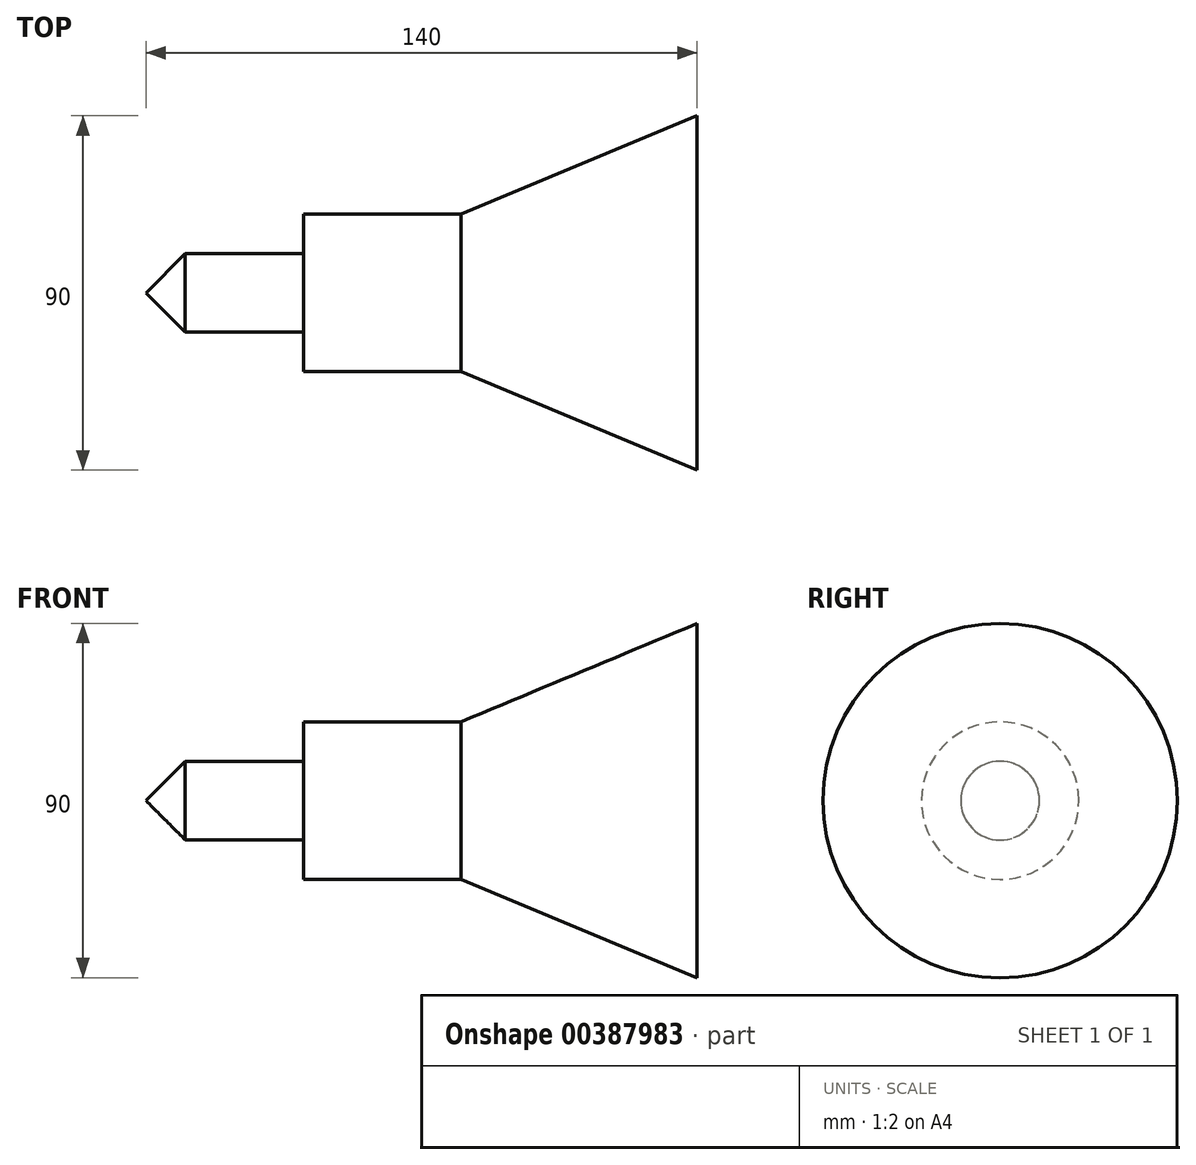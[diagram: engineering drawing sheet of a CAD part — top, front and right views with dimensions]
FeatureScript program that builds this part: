
annotation { "Feature Type Name" : "Feature", "Feature Type Description" : "" }
export const myFeature = defineFeature(function(context is Context, id is Id, definition is map)
    precondition{}
    {
        {
            var Q0;
            Q0=qCreatedBy(makeId("Front.planeOp"),FACE);
            var sketch = newSketch(context, id + "F0", { "sketchPlane" : qUnion([Q0])});
            skLineSegment(sketch, "E0", {"start": v(0, 0) * mm, "end": v(10, 0) * mm});
            skLineSegment(sketch, "E1", {"start": v(10, 0) * mm, "end": v(40, 0) * mm});
            skLineSegment(sketch, "E2", {"start": v(40, 0) * mm, "end": v(80, 0) * mm});
            skLineSegment(sketch, "E3", {"start": v(80, 0) * mm, "end": v(140, 0) * mm});
            skLineSegment(sketch, "E4", {"start": v(10, 0) * mm, "end": v(10, -10) * mm, "construction": true});
            skLineSegment(sketch, "E5", {"start": v(40, 0) * mm, "end": v(40, -20) * mm, "construction": true});
            skLineSegment(sketch, "E6", {"start": v(110, 0) * mm, "end": v(110, -32.5) * mm, "construction": true});
            skLineSegment(sketch, "E7", {"start": v(0, 0) * mm, "end": v(10, -10) * mm});
            skLineSegment(sketch, "E8", {"start": v(10, -10) * mm, "end": v(40, -10) * mm});
            skLineSegment(sketch, "E9", {"start": v(40, -20) * mm, "end": v(80, -20) * mm});
            skLineSegment(sketch, "E10", {"start": v(80, -20) * mm, "end": v(110, -32.5) * mm});
            skLineSegment(sketch, "E11", {"start": v(110, -32.5) * mm, "end": v(140, -45) * mm});
            skLineSegment(sketch, "E12", {"start": v(40, -10) * mm, "end": v(40, -20) * mm});
            skLineSegment(sketch, "E13", {"start": v(140, -45) * mm, "end": v(140, 0) * mm});
            skSolve(sketch);
        }
        {
            var Q0;
            Q0=qCreatedBy(makeId("Front.planeOp"),FACE);
            var sketch = newSketch(context, id + "F1", { "sketchPlane" : qUnion([Q0])});
            skLineSegment(sketch, "E14", {"start": v(0, 0) * mm, "end": v(182.66, 0) * mm, "construction": true});
            skSolve(sketch);
        }
        {
            var Q0;
            Q0 = qSketchRegion(id + "F0", true);
            var Q1;
            Q1=sQuery(id+"F1.wireOp",EDGE,"E14");
            revolve(context, id + "F2", {"entities" : qUnion([Q0]), "axis" : qUnion([Q1]), "revolveType" : RevolveType.FULL});
        }
    });
